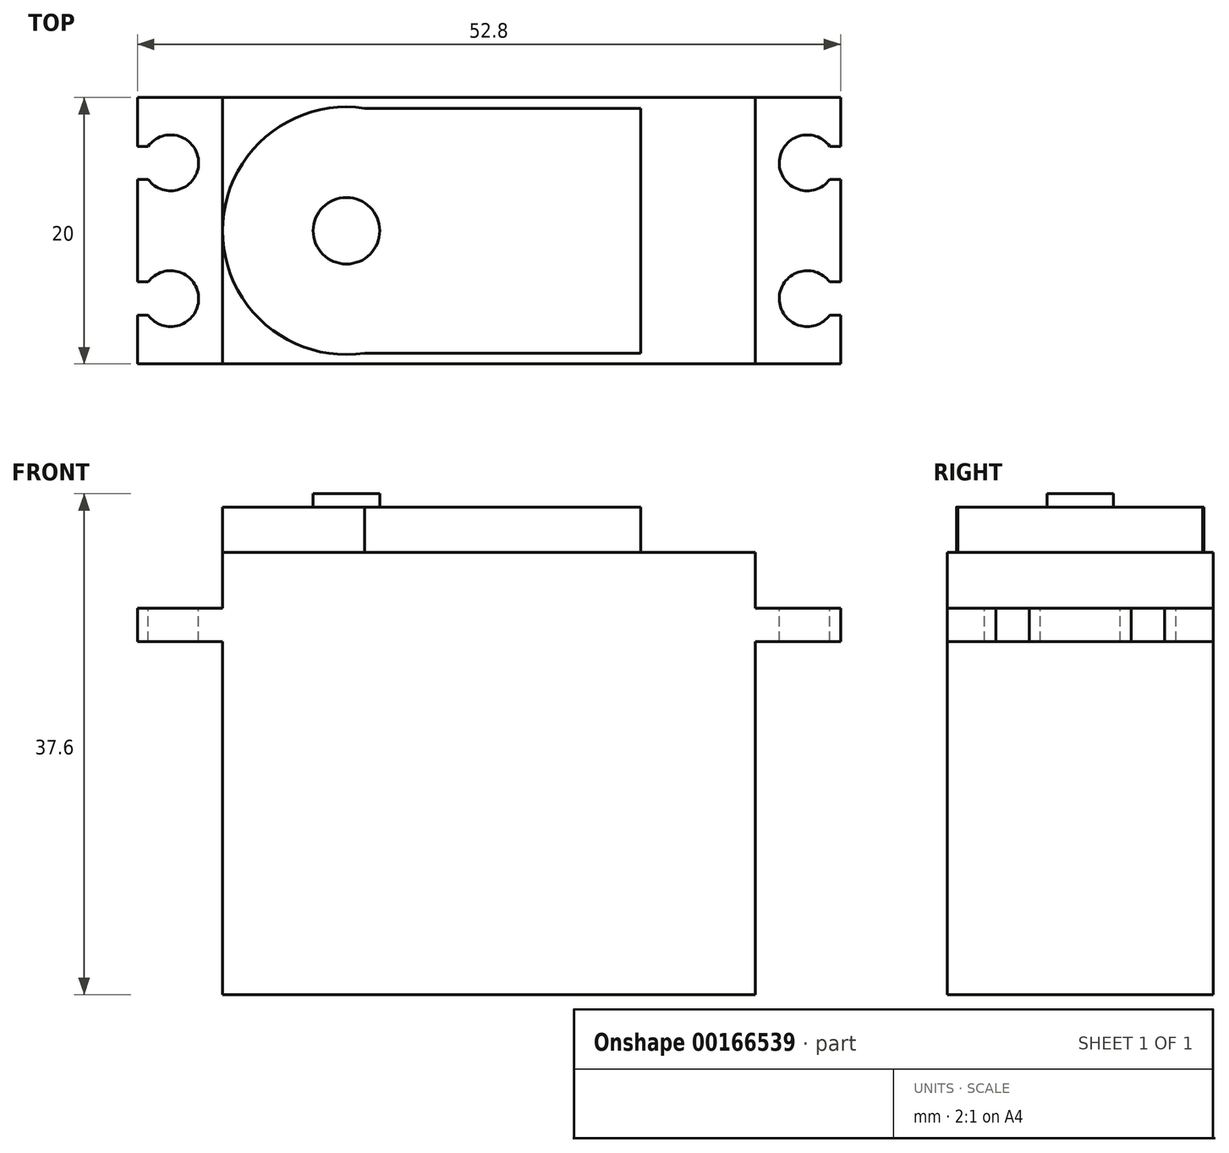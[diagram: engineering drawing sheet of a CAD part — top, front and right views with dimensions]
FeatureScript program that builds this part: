
annotation { "Feature Type Name" : "Feature", "Feature Type Description" : "" }
export const myFeature = defineFeature(function(context is Context, id is Id, definition is map)
    precondition{}
    {
        {
            var Q0;
            Q0=qCreatedBy(makeId("Top.planeOp"),FACE);
            var sketch = newSketch(context, id + "F0", { "sketchPlane" : qUnion([Q0])});
            skLineSegment(sketch, "E0.bottom", {"start": v(-432.7, -254) * mm, "end": v(432.7, -254) * mm});
            skLineSegment(sketch, "E0.top", {"start": v(-432.7, 254) * mm, "end": v(432.7, 254) * mm});
            skLineSegment(sketch, "E0.left", {"start": v(-432.7, -254) * mm, "end": v(-432.7, 254) * mm});
            skLineSegment(sketch, "E0.right", {"start": v(432.7, -254) * mm, "end": v(432.7, 254) * mm});
            skPoint(sketch, "E0.middle", {"position": v(0, 0) * mm});
            skLineSegment(sketch, "E1.bottom", {"start": v(20, -10) * mm, "end": v(-20, -10) * mm});
            skLineSegment(sketch, "E1.top", {"start": v(20, 10) * mm, "end": v(-20, 10) * mm});
            skLineSegment(sketch, "E1.left", {"start": v(20, -10) * mm, "end": v(20, 10) * mm});
            skLineSegment(sketch, "E1.right", {"start": v(-20, -10) * mm, "end": v(-20, 10) * mm});
            skSolve(sketch);
        }
        {
            var Q0;
            Q0=makeQuery(id+"F0.imprint","IMPRINT",FACE,{"disambiguationData":[TD([[makeQuery(id+"F0.imprint","IMPRINT",EDGE,{"derivedFrom":sQuery(id+"F0.wireOp",EDGE,"E1.bottom")}),-1.0]])]});
            extrude(context, id + "F1", {"entities" : qUnion([Q0]), "depth" : 26.5 * mm});
        }
        {
            var Q0;
            Q0=makeQuery(id+"F1.opExtrude","CAP_FACE",FACE,{"disambiguationData":[OSD([sQuery(id+"F0.wireOp",EDGE,"E1.bottom"),sQuery(id+"F0.wireOp",EDGE,"E1.top"),sQuery(id+"F0.wireOp",EDGE,"E1.left"),sQuery(id+"F0.wireOp",EDGE,"E1.right")])],"isStart":false});
            var sketch = newSketch(context, id + "F2", { "sketchPlane" : qUnion([Q0])});
            skLineSegment(sketch, "E2.bottom", {"start": v(26.4, -10) * mm, "end": v(-26.4, -10) * mm});
            skLineSegment(sketch, "E2.top", {"start": v(26.4, 10) * mm, "end": v(-26.4, 10) * mm});
            skLineSegment(sketch, "E2.left", {"start": v(26.4, -10) * mm, "end": v(26.4, 10) * mm});
            skLineSegment(sketch, "E2.right", {"start": v(-26.4, -10) * mm, "end": v(-26.4, 10) * mm});
            skPoint(sketch, "E2.middle", {"position": v(0, 0) * mm});
            skSolve(sketch);
        }
        {
            var Q0;
            Q0=qSketchRegion(id+"F2",true);
            extrude(context, id + "F3", {"entities" : qUnion([Q0]), "operationType" : NewBodyOperationType.ADD, "depth" : 2.5 * mm});
        }
        {
            var Q0;
            Q0=makeQuery(id+"F3.opExtrude","CAP_FACE",FACE,{"disambiguationData":[OSD([sQuery(id+"F2.wireOp",EDGE,"E2.bottom"),sQuery(id+"F2.wireOp",EDGE,"E2.top"),sQuery(id+"F2.wireOp",EDGE,"E2.left"),sQuery(id+"F2.wireOp",EDGE,"E2.right")])],"isStart":false});
            var sketch = newSketch(context, id + "F4", { "sketchPlane" : qUnion([Q0])});
            skLineSegment(sketch, "E3.bottom", {"start": v(20, -10) * mm, "end": v(-20, -10) * mm});
            skLineSegment(sketch, "E3.top", {"start": v(20, 10) * mm, "end": v(-20, 10) * mm});
            skLineSegment(sketch, "E3.left", {"start": v(20, -10) * mm, "end": v(20, 10) * mm});
            skLineSegment(sketch, "E3.right", {"start": v(-20, -10) * mm, "end": v(-20, 10) * mm});
            skPoint(sketch, "E3.middle", {"position": v(0, 0) * mm});
            skSolve(sketch);
        }
        {
            var Q0;
            Q0=makeQuery(id+"F4.imprint","IMPRINT",FACE,{"disambiguationData":[TD([[makeQuery(id+"F4.imprint","IMPRINT",EDGE,{"derivedFrom":sQuery(id+"F4.wireOp",EDGE,"E3.bottom")}),-1.0]])]});
            extrude(context, id + "F5", {"entities" : qUnion([Q0]), "operationType" : NewBodyOperationType.ADD, "depth" : 4.2 * mm});
        }
        {
            var Q0;
            Q0=makeQuery(id+"F5.opExtrude","CAP_FACE",FACE,{"disambiguationData":[OSD([sQuery(id+"F4.wireOp",EDGE,"E3.bottom"),sQuery(id+"F4.wireOp",EDGE,"E3.top"),sQuery(id+"F4.wireOp",EDGE,"E3.left"),sQuery(id+"F4.wireOp",EDGE,"E3.right")])],"isStart":false});
            var sketch = newSketch(context, id + "F6", { "sketchPlane" : qUnion([Q0])});
            skCircle(sketch, "E4", {"center": v(-10.7, 0) * mm, "radius": 9.3 * mm});
            skLineSegment(sketch, "E5.bottom", {"start": v(-10.7, 9.2) * mm, "end": v(11.4, 9.2) * mm});
            skLineSegment(sketch, "E5.top", {"start": v(-10.7, -9.2) * mm, "end": v(11.4, -9.2) * mm});
            skLineSegment(sketch, "E5.left", {"start": v(-10.7, 9.2) * mm, "end": v(-10.7, -9.2) * mm});
            skLineSegment(sketch, "E5.right", {"start": v(11.4, 9.2) * mm, "end": v(11.4, -9.2) * mm});
            skSolve(sketch);
        }
        {
            var Q0;
            {var subQ0=sQuery(id+"F6.wireOp",EDGE,"E5.left");Q0=makeQuery(id+"F6.imprint","IMPRINT",FACE,{"disambiguationData":[TD([[makeQuery(id+"F6.imprint","IMPRINT",EDGE,{"derivedFrom":subQ0}),-1.0]])]});}
            var Q1;
            {var subQ5=sQuery(id+"F6.wireOp",EDGE,"E5.left");Q1=makeQuery(id+"F6.imprint","IMPRINT",FACE,{"disambiguationData":[TD([[makeQuery(id+"F6.imprint","IMPRINT",EDGE,{"derivedFrom":subQ5}),1.0]])]});}
            var Q2;
            {var subQ5=sQuery(id+"F6.wireOp",EDGE,"E5.right");Q2=makeQuery(id+"F6.imprint","IMPRINT",FACE,{"disambiguationData":[TD([[makeQuery(id+"F6.imprint","IMPRINT",EDGE,{"derivedFrom":subQ5}),-1.0]])]});}
            extrude(context, id + "F7", {"entities" : qUnion([Q0, Q1, Q2]), "operationType" : NewBodyOperationType.ADD, "depth" : 3.4 * mm});
        }
        {
            var Q0;
            Q0=makeQuery(id+"F7.opExtrude","CAP_FACE",FACE,{"disambiguationData":[OSD([sQuery(id+"F6.wireOp",EDGE,"E4"),sQuery(id+"F6.wireOp",EDGE,"E5.bottom"),sQuery(id+"F6.wireOp",EDGE,"E5.top"),sQuery(id+"F6.wireOp",EDGE,"E5.right")])],"isStart":false});
            var sketch = newSketch(context, id + "F8", { "sketchPlane" : qUnion([Q0])});
            skCircle(sketch, "E6", {"center": v(-10.7, 0) * mm, "radius": 2.5 * mm});
            skSolve(sketch);
        }
        {
            var Q0;
            Q0=makeQuery(id+"F8.imprint","IMPRINT",FACE,{"disambiguationData":[TD([[makeQuery(id+"F8.imprint","IMPRINT",EDGE,{"derivedFrom":sQuery(id+"F8.wireOp",EDGE,"E6")}),1.0]])]});
            extrude(context, id + "F9", {"entities" : qUnion([Q0]), "operationType" : NewBodyOperationType.ADD, "depth" : 1 * mm});
        }
        {
            var Q0;
            {var subQ0=sQuery(id+"F2.wireOp",EDGE,"E2.top");var subQ1=sQuery(id+"F2.wireOp",EDGE,"E2.bottom");var subQ2=sQuery(id+"F2.wireOp",EDGE,"E2.right");Q0=makeQuery(id+"F5.boolean.opBoolean","SPLIT",FACE,{"disambiguationData":[TD([makeQuery(id+"F3.opExtrude","SWEPT_FACE",FACE,{"disambiguationData":[OSD([subQ2])]})])],"derivedFrom":makeQuery(id+"F3.opExtrude","CAP_FACE",FACE,{"disambiguationData":[OSD([subQ1,subQ0,sQuery(id+"F2.wireOp",EDGE,"E2.left"),subQ2])],"isStart":false})});}
            var sketch = newSketch(context, id + "F10", { "sketchPlane" : qUnion([Q0])});
            skLineSegment(sketch, "E7.bottom", {"start": v(-23.9, 5.1) * mm, "end": v(23.9, 5.1) * mm});
            skLineSegment(sketch, "E7.top", {"start": v(-23.9, -5.1) * mm, "end": v(23.9, -5.1) * mm});
            skLineSegment(sketch, "E7.left", {"start": v(-23.9, 5.1) * mm, "end": v(-23.9, -5.1) * mm});
            skLineSegment(sketch, "E7.right", {"start": v(23.9, 5.1) * mm, "end": v(23.9, -5.1) * mm});
            skPoint(sketch, "E7.middle", {"position": v(0, 0) * mm});
            skCircle(sketch, "E8", {"center": v(-23.9, 5.1) * mm, "radius": 2.1 * mm});
            skCircle(sketch, "E9", {"center": v(-23.9, -5.1) * mm, "radius": 2.1 * mm});
            skCircle(sketch, "E10", {"center": v(23.9, 5.1) * mm, "radius": 2.1 * mm});
            skCircle(sketch, "E11", {"center": v(23.9, -5.1) * mm, "radius": 2.1 * mm});
            skLineSegment(sketch, "E12.bottom", {"start": v(-27.25, 3.84) * mm, "end": v(-24.75, 3.84) * mm});
            skLineSegment(sketch, "E12.top", {"start": v(-27.25, 6.34) * mm, "end": v(-24.75, 6.34) * mm});
            skLineSegment(sketch, "E12.left", {"start": v(-27.25, 3.84) * mm, "end": v(-27.25, 6.34) * mm});
            skLineSegment(sketch, "E12.right", {"start": v(-24.75, 3.84) * mm, "end": v(-24.75, 6.34) * mm});
            skPoint(sketch, "E12.middle", {"position": v(-26, 5.09) * mm});
            skLineSegment(sketch, "E13.bottom", {"start": v(-27.25, -6.34) * mm, "end": v(-24.75, -6.34) * mm});
            skLineSegment(sketch, "E13.top", {"start": v(-27.25, -3.84) * mm, "end": v(-24.75, -3.84) * mm});
            skLineSegment(sketch, "E13.left", {"start": v(-27.25, -6.34) * mm, "end": v(-27.25, -3.84) * mm});
            skLineSegment(sketch, "E13.right", {"start": v(-24.75, -6.34) * mm, "end": v(-24.75, -3.84) * mm});
            skPoint(sketch, "E13.middle", {"position": v(-26, -5.09) * mm});
            skLineSegment(sketch, "E14.bottom", {"start": v(27.25, 3.84) * mm, "end": v(24.75, 3.84) * mm});
            skLineSegment(sketch, "E14.top", {"start": v(27.25, 6.34) * mm, "end": v(24.75, 6.34) * mm});
            skLineSegment(sketch, "E14.left", {"start": v(27.25, 3.84) * mm, "end": v(27.25, 6.34) * mm});
            skLineSegment(sketch, "E14.right", {"start": v(24.75, 3.84) * mm, "end": v(24.75, 6.34) * mm});
            skPoint(sketch, "E14.middle", {"position": v(26, 5.09) * mm});
            skLineSegment(sketch, "E15.bottom", {"start": v(27.25, -6.34) * mm, "end": v(24.75, -6.34) * mm});
            skLineSegment(sketch, "E15.top", {"start": v(27.25, -3.84) * mm, "end": v(24.75, -3.84) * mm});
            skLineSegment(sketch, "E15.left", {"start": v(27.25, -6.34) * mm, "end": v(27.25, -3.84) * mm});
            skLineSegment(sketch, "E15.right", {"start": v(24.75, -6.34) * mm, "end": v(24.75, -3.84) * mm});
            skPoint(sketch, "E15.middle", {"position": v(26, -5.09) * mm});
            skSolve(sketch);
        }
        {
            var Q0;
            {var subQ10=sQuery(id+"F10.wireOp",EDGE,"E12.right");Q0=makeQuery(id+"F10.imprint","IMPRINT",FACE,{"disambiguationData":[TD([[makeQuery(id+"F10.imprint","IMPRINT",EDGE,{"derivedFrom":subQ10}),-1.0]])]});}
            var Q1;
            {var subQ0=sQuery(id+"F10.wireOp",EDGE,"E7.left");var subQ1=sQuery(id+"F10.wireOp",EDGE,"E7.bottom");var subQ2=makeQuery(id+"F10.imprint","INTERSECT",VERTEX,{"derivedFrom":[subQ1,subQ0]});Q1=makeQuery(id+"F10.imprint","IMPRINT",FACE,{"disambiguationData":[TD([[makeQuery(id+"F10.imprint","IMPRINT",EDGE,{"disambiguationData":[TD([[subQ2,-1.0]])],"derivedFrom":subQ1}),-1.0]])]});}
            var Q2;
            {var subQ5=sQuery(id+"F10.wireOp",EDGE,"E12.right");Q2=makeQuery(id+"F10.imprint","IMPRINT",FACE,{"disambiguationData":[TD([[makeQuery(id+"F10.imprint","IMPRINT",EDGE,{"derivedFrom":subQ5}),1.0]])]});}
            var Q3;
            {var subQ10=sQuery(id+"F10.wireOp",EDGE,"E13.right");Q3=makeQuery(id+"F10.imprint","IMPRINT",FACE,{"disambiguationData":[TD([[makeQuery(id+"F10.imprint","IMPRINT",EDGE,{"derivedFrom":subQ10}),-1.0]])]});}
            var Q4;
            {var subQ0=sQuery(id+"F10.wireOp",EDGE,"E7.left");var subQ1=sQuery(id+"F10.wireOp",EDGE,"E7.top");var subQ2=makeQuery(id+"F10.imprint","INTERSECT",VERTEX,{"derivedFrom":[subQ1,subQ0]});Q4=makeQuery(id+"F10.imprint","IMPRINT",FACE,{"disambiguationData":[TD([[makeQuery(id+"F10.imprint","IMPRINT",EDGE,{"disambiguationData":[TD([[subQ2,-1.0]])],"derivedFrom":subQ1}),1.0]])]});}
            var Q5;
            {var subQ5=sQuery(id+"F10.wireOp",EDGE,"E13.right");Q5=makeQuery(id+"F10.imprint","IMPRINT",FACE,{"disambiguationData":[TD([[makeQuery(id+"F10.imprint","IMPRINT",EDGE,{"derivedFrom":subQ5}),1.0]])]});}
            var Q6;
            {var subQ5=sQuery(id+"F10.wireOp",EDGE,"E14.right");Q6=makeQuery(id+"F10.imprint","IMPRINT",FACE,{"disambiguationData":[TD([[makeQuery(id+"F10.imprint","IMPRINT",EDGE,{"derivedFrom":subQ5}),-1.0]])]});}
            var Q7;
            {var subQ5=sQuery(id+"F10.wireOp",EDGE,"E14.right");Q7=makeQuery(id+"F10.imprint","IMPRINT",FACE,{"disambiguationData":[TD([[makeQuery(id+"F10.imprint","IMPRINT",EDGE,{"derivedFrom":subQ5}),1.0]])]});}
            var Q8;
            {var subQ0=sQuery(id+"F10.wireOp",EDGE,"E7.right");var subQ1=sQuery(id+"F10.wireOp",EDGE,"E7.bottom");var subQ2=makeQuery(id+"F10.imprint","INTERSECT",VERTEX,{"derivedFrom":[subQ1,subQ0]});Q8=makeQuery(id+"F10.imprint","IMPRINT",FACE,{"disambiguationData":[TD([[makeQuery(id+"F10.imprint","IMPRINT",EDGE,{"disambiguationData":[TD([[subQ2,1.0]])],"derivedFrom":subQ1}),-1.0]])]});}
            var Q9;
            {var subQ5=sQuery(id+"F10.wireOp",EDGE,"E14.left");Q9=makeQuery(id+"F10.imprint","IMPRINT",FACE,{"disambiguationData":[TD([[makeQuery(id+"F10.imprint","IMPRINT",EDGE,{"derivedFrom":subQ5}),1.0]])]});}
            var Q10;
            {var subQ5=sQuery(id+"F10.wireOp",EDGE,"E15.left");Q10=makeQuery(id+"F10.imprint","IMPRINT",FACE,{"disambiguationData":[TD([[makeQuery(id+"F10.imprint","IMPRINT",EDGE,{"derivedFrom":subQ5}),1.0]])]});}
            var Q11;
            {var subQ5=sQuery(id+"F10.wireOp",EDGE,"E15.right");Q11=makeQuery(id+"F10.imprint","IMPRINT",FACE,{"disambiguationData":[TD([[makeQuery(id+"F10.imprint","IMPRINT",EDGE,{"derivedFrom":subQ5}),1.0]])]});}
            var Q12;
            {var subQ0=sQuery(id+"F10.wireOp",EDGE,"E7.right");var subQ1=sQuery(id+"F10.wireOp",EDGE,"E7.top");var subQ2=makeQuery(id+"F10.imprint","INTERSECT",VERTEX,{"derivedFrom":[subQ1,subQ0]});Q12=makeQuery(id+"F10.imprint","IMPRINT",FACE,{"disambiguationData":[TD([[makeQuery(id+"F10.imprint","IMPRINT",EDGE,{"disambiguationData":[TD([[subQ2,1.0]])],"derivedFrom":subQ1}),1.0]])]});}
            var Q13;
            {var subQ5=sQuery(id+"F10.wireOp",EDGE,"E15.right");Q13=makeQuery(id+"F10.imprint","IMPRINT",FACE,{"disambiguationData":[TD([[makeQuery(id+"F10.imprint","IMPRINT",EDGE,{"derivedFrom":subQ5}),-1.0]])]});}
            var Q14;
            {var subQ0=sQuery(id+"F10.wireOp",EDGE,"E13.top");var subQ1=sQuery(id+"F10.wireOp",EDGE,"E9");var subQ2=makeQuery(id+"F10.imprint","INTERSECT",VERTEX,{"derivedFrom":[subQ1,subQ0]});Q14=makeQuery(id+"F10.imprint","IMPRINT",FACE,{"disambiguationData":[TD([[makeQuery(id+"F10.imprint","IMPRINT",EDGE,{"disambiguationData":[TD([[subQ2,-1.0]])],"derivedFrom":subQ1}),-1.0]])]});}
            var Q15;
            {var subQ0=sQuery(id+"F10.wireOp",EDGE,"E12.top");var subQ1=sQuery(id+"F10.wireOp",EDGE,"E8");var subQ2=makeQuery(id+"F10.imprint","INTERSECT",VERTEX,{"derivedFrom":[subQ1,subQ0]});Q15=makeQuery(id+"F10.imprint","IMPRINT",FACE,{"disambiguationData":[TD([[makeQuery(id+"F10.imprint","IMPRINT",EDGE,{"disambiguationData":[TD([[subQ2,-1.0]])],"derivedFrom":subQ1}),-1.0]])]});}
            extrude(context, id + "F11", {"entities" : qUnion([Q0, Q1, Q2, Q3, Q4, Q5, Q6, Q7, Q8, Q9, Q10, Q11, Q12, Q13, Q14, Q15]), "operationType" : NewBodyOperationType.REMOVE, "endBound" : BoundingType.THROUGH_ALL, "oppositeDirection" : true, "depth" : 25 * mm});
        }
    });
